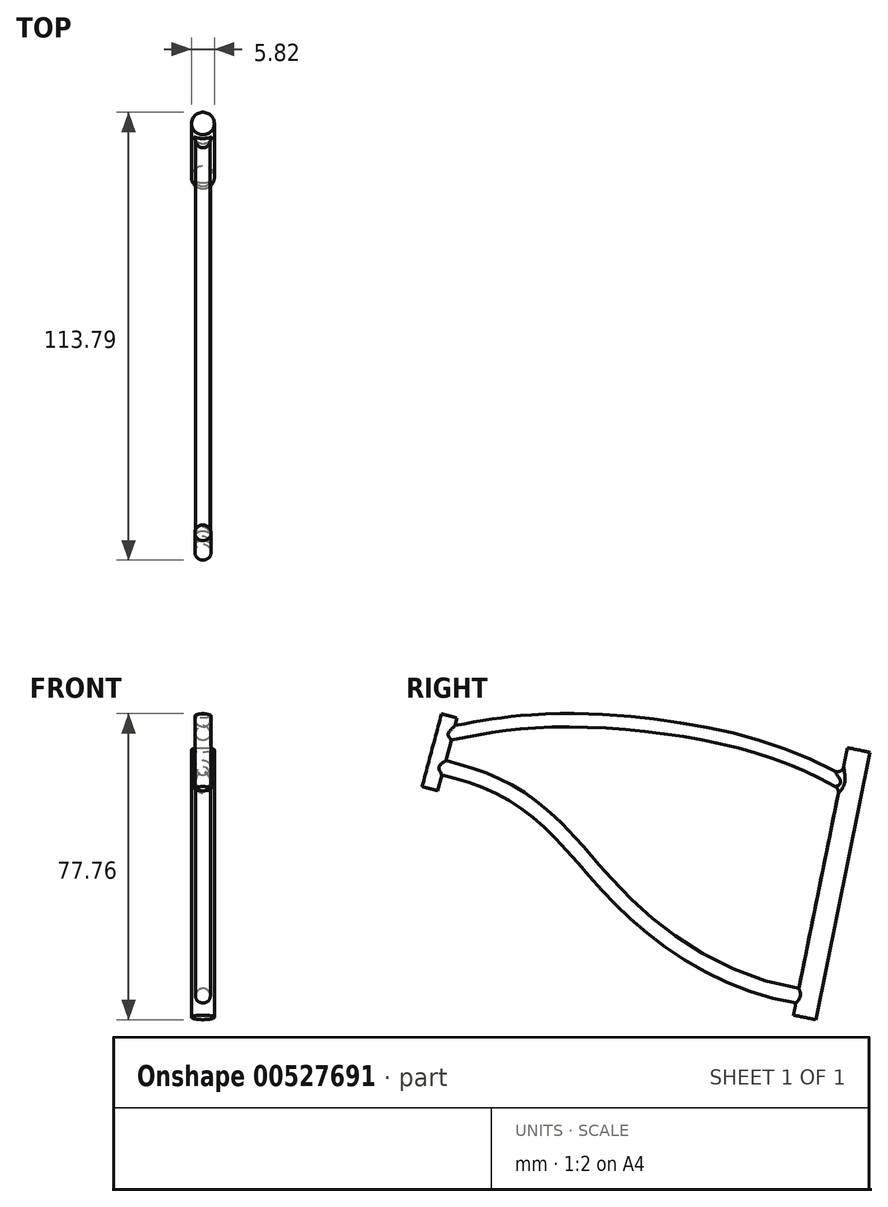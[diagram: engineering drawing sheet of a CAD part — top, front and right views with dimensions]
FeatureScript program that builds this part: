
annotation { "Feature Type Name" : "Feature", "Feature Type Description" : "" }
export const myFeature = defineFeature(function(context is Context, id is Id, definition is map)
    precondition{}
    {
        {
            var Q0;
            Q0=qCreatedBy(makeId("Right.planeOp"),FACE);
            var sketch = newSketch(context, id + "F0", { "sketchPlane" : qUnion([Q0])});
            skLineSegment(sketch, "E0", {"start": v(-60.5, 24.58) * mm, "end": v(-65.44, 6.1) * mm});
            skLineSegment(sketch, "E1", {"start": v(43.5, 15.94) * mm, "end": v(29.8, -52) * mm});
            skFitSpline(sketch, "E2", {"points": [v(-61.74, 19.91) * mm, v(-36.95, 23.4) * mm, v(5.75, 19.84) * mm, v(41.55, 6.26) * mm], "startDerivative": vector(88.13, 16.99) * mm, "endDerivative": vector(92.25, -56.97) * mm});
            skFitSpline(sketch, "E3", {"points": [v(-63.9, 11.88) * mm, v(-46.78, 6.1) * mm, v(-30.7, -6.7) * mm, v(-9.83, -28.46) * mm, v(30.85, -46.78) * mm], "startDerivative": vector(75.17, -16) * mm, "endDerivative": vector(136.98, -11.1) * mm});
            skLineSegment(sketch, "E4", {"start": v(43.5, 15.94) * mm, "end": v(31.16, 18.43) * mm});
            skLineSegment(sketch, "E5", {"start": v(-60.5, 24.58) * mm, "end": v(-70.16, 27.17) * mm});
            skSolve(sketch);
        }
        {
            var Q0;
            Q0=sQuery(id+"F0.wireOp",EDGE,"E4");
            var Q1;
            Q1=sQuery(id+"F0.wireOp",EDGE,"E5");
            extrude(context, id + "F1", {"bodyType" : ToolBodyType.SURFACE, "surfaceEntities" : qUnion([Q0, Q1]), "endBound" : BoundingType.SYMMETRIC, "depth" : 25.4 * mm, "offsetDistance" : 25.4 * mm});
        }
        {
            var Q0;
            Q0=makeQuery(id+"F1.opExtrude","SWEPT_FACE",FACE,{"disambiguationData":[OSD([sQuery(id+"F0.wireOp",EDGE,"E4")])]});
            var sketch = newSketch(context, id + "F2", { "sketchPlane" : qUnion([Q0])});
            skCircle(sketch, "E6", {"center": v(0, 39.5) * mm, "radius": 2.91 * mm});
            skSolve(sketch);
        }
        {
            var Q0;
            {var subQ0=sQuery(id+"F2.wireOp",EDGE,"E6");var subQ1=makeQuery(id+"F1.opExtrude","SWEPT_EDGE",EDGE,{"disambiguationData":[OSD([sQuery(id+"F0.wireOp",VERTEX,"E4.start")])]});var subQ2=makeQuery(id+"F2.imprint","INTERSECT",VERTEX,{"disambiguationData":[OD(0.0)],"derivedFrom":[subQ1,subQ0]});Q0=makeQuery(id+"F2.imprint","IMPRINT",FACE,{"disambiguationData":[TD([[makeQuery(id+"F2.imprint","IMPRINT",EDGE,{"disambiguationData":[TD([[subQ2,1.0]])],"derivedFrom":subQ0}),1.0]])]});}
            var Q1;
            {var subQ0=sQuery(id+"F2.wireOp",EDGE,"E6");var subQ1=makeQuery(id+"F1.opExtrude","SWEPT_EDGE",EDGE,{"disambiguationData":[OSD([sQuery(id+"F0.wireOp",VERTEX,"E4.start")])]});var subQ2=makeQuery(id+"F2.imprint","INTERSECT",VERTEX,{"disambiguationData":[OD(0.0)],"derivedFrom":[subQ1,subQ0]});Q1=makeQuery(id+"F2.imprint","IMPRINT",FACE,{"disambiguationData":[TD([[makeQuery(id+"F2.imprint","IMPRINT",EDGE,{"disambiguationData":[TD([[subQ2,-1.0]])],"derivedFrom":subQ0}),1.0]])]});}
            var Q2;
            Q2=sQuery(id+"F0.wireOp",EDGE,"E1");
            sweep(context, id + "F3", {"profiles" : qUnion([Q0, Q1]), "path" : qUnion([Q2])});
        }
        {
            var Q0;
            Q0=makeQuery(id+"F1.opExtrude","SWEPT_FACE",FACE,{"disambiguationData":[OSD([sQuery(id+"F0.wireOp",EDGE,"E5")])]});
            var sketch = newSketch(context, id + "F4", { "sketchPlane" : qUnion([Q0])});
            skCircle(sketch, "E7", {"center": v(0, -64.8) * mm, "radius": 2.06 * mm});
            skSolve(sketch);
        }
        {
            var Q0;
            {var subQ0=sQuery(id+"F4.wireOp",EDGE,"E7");var subQ1=makeQuery(id+"F1.opExtrude","SWEPT_EDGE",EDGE,{"disambiguationData":[OSD([sQuery(id+"F0.wireOp",VERTEX,"E5.start")])]});var subQ2=makeQuery(id+"F4.imprint","INTERSECT",VERTEX,{"disambiguationData":[OD(0.0)],"derivedFrom":[subQ1,subQ0]});Q0=makeQuery(id+"F4.imprint","IMPRINT",FACE,{"disambiguationData":[TD([[makeQuery(id+"F4.imprint","IMPRINT",EDGE,{"disambiguationData":[TD([[subQ2,1.0]])],"derivedFrom":subQ0}),1.0]])]});}
            var Q1;
            {var subQ0=sQuery(id+"F4.wireOp",EDGE,"E7");var subQ1=makeQuery(id+"F1.opExtrude","SWEPT_EDGE",EDGE,{"disambiguationData":[OSD([sQuery(id+"F0.wireOp",VERTEX,"E5.start")])]});var subQ2=makeQuery(id+"F4.imprint","INTERSECT",VERTEX,{"disambiguationData":[OD(0.0)],"derivedFrom":[subQ1,subQ0]});Q1=makeQuery(id+"F4.imprint","IMPRINT",FACE,{"disambiguationData":[TD([[makeQuery(id+"F4.imprint","IMPRINT",EDGE,{"disambiguationData":[TD([[subQ2,-1.0]])],"derivedFrom":subQ0}),1.0]])]});}
            var Q2;
            Q2=sQuery(id+"F0.wireOp",EDGE,"E0");
            sweep(context, id + "F5", {"profiles" : qUnion([Q0, Q1]), "path" : qUnion([Q2])});
        }
        {
            var Q0;
            Q0=sQuery(id+"F0.wireOp",EDGE,"E0");
            var Q1;
            Q1=sQuery(id+"F0.wireOp",EDGE,"E1");
            extrude(context, id + "F6", {"bodyType" : ToolBodyType.SURFACE, "surfaceEntities" : qUnion([Q0, Q1]), "endBound" : BoundingType.SYMMETRIC, "depth" : 25.4 * mm, "offsetDistance" : 25.4 * mm});
        }
        {
            var Q0;
            Q0=makeQuery(id+"F6.opExtrude","SWEPT_FACE",FACE,{"disambiguationData":[OSD([sQuery(id+"F0.wireOp",EDGE,"E0")])]});
            var sketch = newSketch(context, id + "F7", { "sketchPlane" : qUnion([Q0])});
            skCircle(sketch, "E8", {"center": v(0, 3.22) * mm, "radius": 1.87 * mm});
            skCircle(sketch, "E9", {"center": v(0, -5.09) * mm, "radius": 1.9 * mm});
            skSolve(sketch);
        }
        {
            var Q0;
            Q0=makeQuery(id+"F7.imprint","IMPRINT",FACE,{"disambiguationData":[TD([[makeQuery(id+"F7.imprint","IMPRINT",EDGE,{"derivedFrom":sQuery(id+"F7.wireOp",EDGE,"E8")}),1.0]])]});
            var Q1;
            Q1=sQuery(id+"F0.wireOp",EDGE,"E2");
            sweep(context, id + "F8", {"profiles" : qUnion([Q0]), "path" : qUnion([Q1])});
        }
        {
            var Q0;
            Q0=makeQuery(id+"F7.imprint","IMPRINT",FACE,{"disambiguationData":[TD([[makeQuery(id+"F7.imprint","IMPRINT",EDGE,{"derivedFrom":sQuery(id+"F7.wireOp",EDGE,"E9")}),1.0]])]});
            var Q1;
            Q1=sQuery(id+"F0.wireOp",EDGE,"E3");
            sweep(context, id + "F9", {"profiles" : qUnion([Q0]), "path" : qUnion([Q1])});
        }
        {
            var Q0;
            Q0=makeQuery(id+"F3.opSweep","SWEPT_BODY",BODY,{"disambiguationData":[OSD([sQuery(id+"F0.wireOp",EDGE,"E1"),sQuery(id+"F2.wireOp",EDGE,"E6")])]});
            var Q1;
            Q1=makeQuery(id+"F8.opSweep","SWEPT_BODY",BODY,{"disambiguationData":[OSD([sQuery(id+"F0.wireOp",EDGE,"E2"),sQuery(id+"F7.wireOp",EDGE,"E8")])]});
            var Q2;
            Q2=makeQuery(id+"F9.opSweep","SWEPT_BODY",BODY,{"disambiguationData":[OSD([sQuery(id+"F0.wireOp",EDGE,"E3"),sQuery(id+"F7.wireOp",EDGE,"E9")])]});
            var Q3;
            Q3=makeQuery(id+"F5.opSweep","SWEPT_BODY",BODY,{"disambiguationData":[OSD([sQuery(id+"F0.wireOp",EDGE,"E0"),sQuery(id+"F4.wireOp",EDGE,"E7")])]});
            booleanBodies(context, id + "F10", {"operationType" : BooleanOperationType.UNION, "tools" : qUnion([Q0, Q1, Q2, Q3])});
        }
        {
            var Q0;
            Q0=makeQuery(id+"F10.opBoolean","INTERSECT",EDGE,{"derivedFrom":[makeQuery(id+"F3.opSweep","SWEPT_FACE",FACE,{"disambiguationData":[OSD([sQuery(id+"F0.wireOp",EDGE,"E1"),sQuery(id+"F2.wireOp",EDGE,"E6")])]}),makeQuery(id+"F8.opSweep","SWEPT_FACE",FACE,{"disambiguationData":[OSD([sQuery(id+"F0.wireOp",EDGE,"E2"),sQuery(id+"F7.wireOp",EDGE,"E8")])]})]});
            fillet(context, id + "F11", {"entities" : qUnion([Q0]), "radius" : 1.62 * mm, "tangentPropagation" : true, "allowEdgeOverflow" : false});
        }
    });
